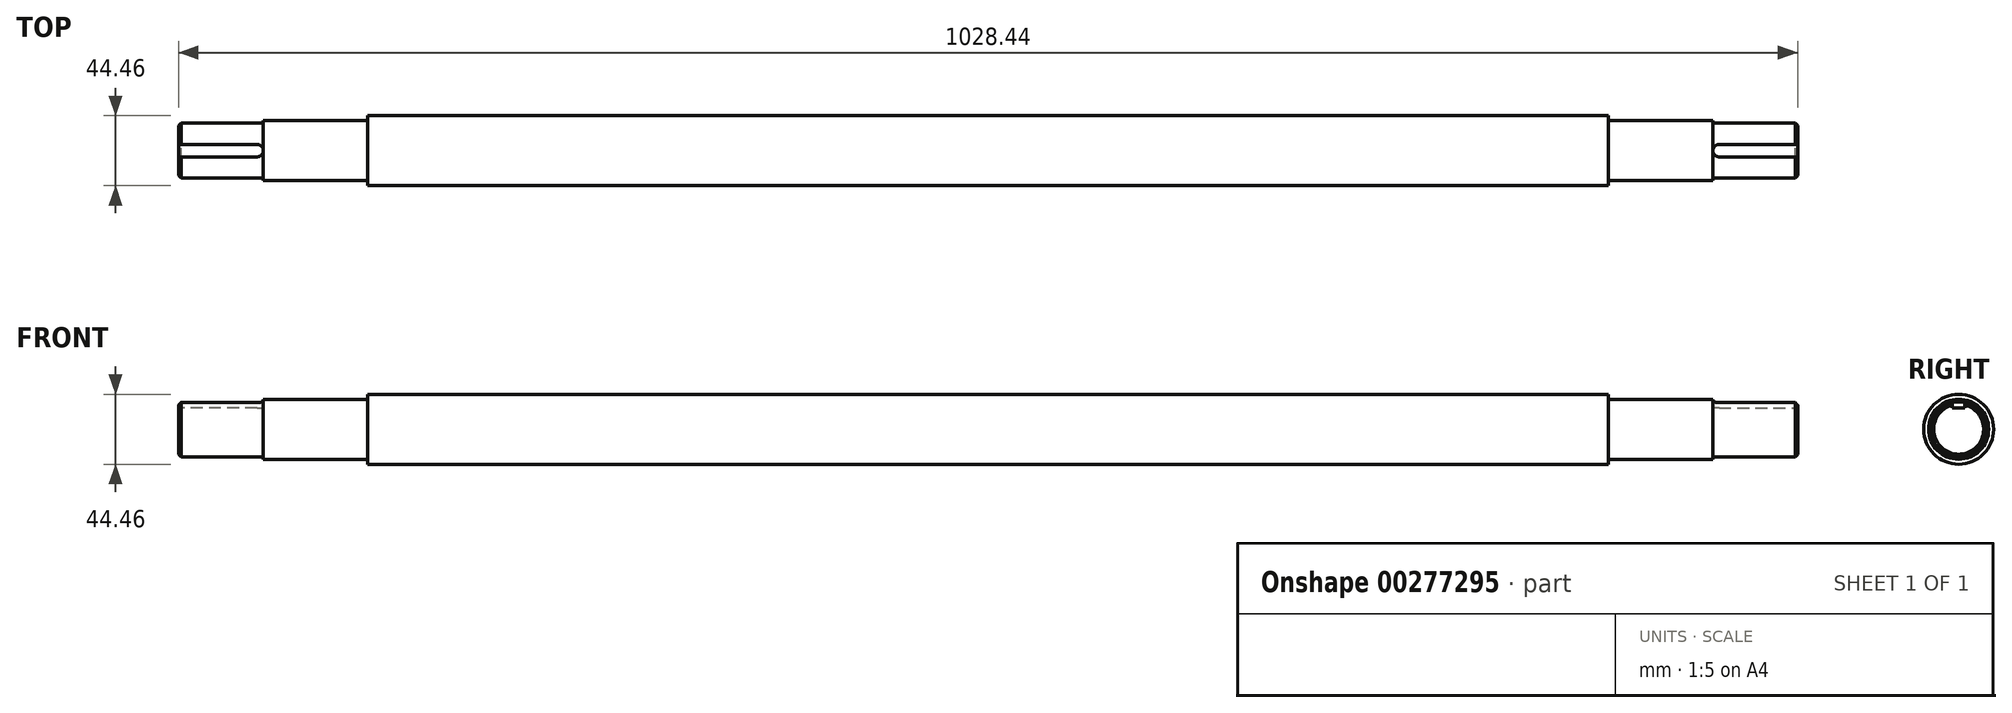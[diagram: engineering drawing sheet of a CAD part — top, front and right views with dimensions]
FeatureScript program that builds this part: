
annotation { "Feature Type Name" : "Feature", "Feature Type Description" : "" }
export const myFeature = defineFeature(function(context is Context, id is Id, definition is map)
    precondition{}
    {
        {
            var Q0;
            Q0=qCreatedBy(makeId("Right.planeOp"),FACE);
            var sketch = newSketch(context, id + "F0", { "sketchPlane" : qUnion([Q0])});
            skCircle(sketch, "E0", {"center": v(0, 0) * mm, "radius": 22.23 * mm});
            skSolve(sketch);
        }
        {
            var Q0;
            Q0 = qSketchRegion(id + "F0", true);
            extrude(context, id + "F1", {"entities" : qUnion([Q0]), "depth" : 394.1 * mm});
        }
        {
            var Q0;
            Q0=makeQuery(id+"F1.opExtrude","CAP_FACE",FACE,{"disambiguationData":[OSD([sQuery(id+"F0.wireOp",EDGE,"E0")])],"isStart":false});
            var sketch = newSketch(context, id + "F2", { "sketchPlane" : qUnion([Q0])});
            skCircle(sketch, "E1", {"center": v(0, 0) * mm, "radius": 19.05 * mm});
            skSolve(sketch);
        }
        {
            var Q0;
            Q0 = qSketchRegion(id + "F2", true);
            extrude(context, id + "F3", {"entities" : qUnion([Q0]), "operationType" : NewBodyOperationType.ADD, "depth" : 66.27 * mm});
        }
        {
            var Q0;
            Q0=makeQuery(id+"F3.opExtrude","CAP_FACE",FACE,{"disambiguationData":[OSD([sQuery(id+"F2.wireOp",EDGE,"E1")])],"isStart":false});
            var sketch = newSketch(context, id + "F4", { "sketchPlane" : qUnion([Q0])});
            skLineSegment(sketch, "E2", {"start": v(0, 0) * mm, "end": v(0, 17.46) * mm, "construction": true});
            skPoint(sketch, "E3.middle", {"position": v(0, 17.46) * mm});
            skPoint(sketch, "E4.orphan", {"position": v(-3.97, 21.27) * mm});
            skPoint(sketch, "E5.orphan", {"position": v(3.97, 21.27) * mm});
            skCircle(sketch, "E6.converted", {"center": v(0, 0) * mm, "radius": 17.46 * mm});
            skSolve(sketch);
        }
        {
            var Q0;
            Q0 = qSketchRegion(id + "F4", true);
            extrude(context, id + "F5", {"entities" : qUnion([Q0]), "operationType" : NewBodyOperationType.ADD, "depth" : 53.85 * mm});
        }
        {
            var Q0;
            Q0=makeQuery(id+"F5.opExtrude","CAP_FACE",FACE,{"disambiguationData":[OSD([sQuery(id+"F4.wireOp",EDGE,"E6.converted")])],"isStart":false});
            chamfer(context, id + "F6", {"entities" : qUnion([Q0]), "width" : 1.59 * mm, "tangentPropagation" : true});
        }
        {
            var Q0;
            Q0=qCreatedBy(makeId("Top.planeOp"),FACE);
            cPlane(context, id + "F7", {"entities" : qUnion([Q0]), "cplaneType" : CPlaneType.OFFSET, "offset" : 17.46 * mm, "width" : 152.4 * mm, "height" : 152.4 * mm});
        }
        {
            var Q0;
            Q0=qCreatedBy(id+"F7.planeOp",FACE);
            var sketch = newSketch(context, id + "F8", { "sketchPlane" : qUnion([Q0])});
            skLineSegment(sketch, "E7.0", {"start": v(514.22, 15.88) * mm, "end": v(514.22, -15.88) * mm, "construction": true});
            skLineSegment(sketch, "E8.0", {"start": v(460.38, 19.05) * mm, "end": v(460.38, -19.05) * mm, "construction": true});
            skLineSegment(sketch, "E9", {"start": v(460.38, 0) * mm, "end": v(464.34, 0) * mm, "construction": true});
            skArc(sketch, "E10", {"start": v(464.34, 3.96) * mm, "mid": v(460.38, 0) * mm, "end": v(464.34, -3.96) * mm});
            skLineSegment(sketch, "E11.bottom", {"start": v(464.34, 3.96) * mm, "end": v(521.66, 3.96) * mm});
            skLineSegment(sketch, "E11.top", {"start": v(464.34, -3.96) * mm, "end": v(521.66, -3.96) * mm});
            skLineSegment(sketch, "E11.right", {"start": v(521.66, 3.96) * mm, "end": v(521.66, -3.96) * mm});
            skSolve(sketch);
        }
        {
            var Q0;
            Q0 = qSketchRegion(id + "F8", true);
            extrude(context, id + "F9", {"entities" : qUnion([Q0]), "operationType" : NewBodyOperationType.REMOVE, "oppositeDirection" : true, "depth" : 3.8 * mm});
        }
        {
            var Q0;
            Q0=makeQuery(id+"F1.opExtrude","SWEPT_BODY",BODY,{"disambiguationData":[OSD([sQuery(id+"F0.wireOp",EDGE,"E0")])]});
            var Q1;
            Q1=qCreatedBy(makeId("Right.planeOp"),FACE);
            mirror(context, id + "F10", {"operationType" : NewBodyOperationType.ADD, "entities" : qUnion([Q0]), "mirrorPlane" : qUnion([Q1])});
        }
    });
